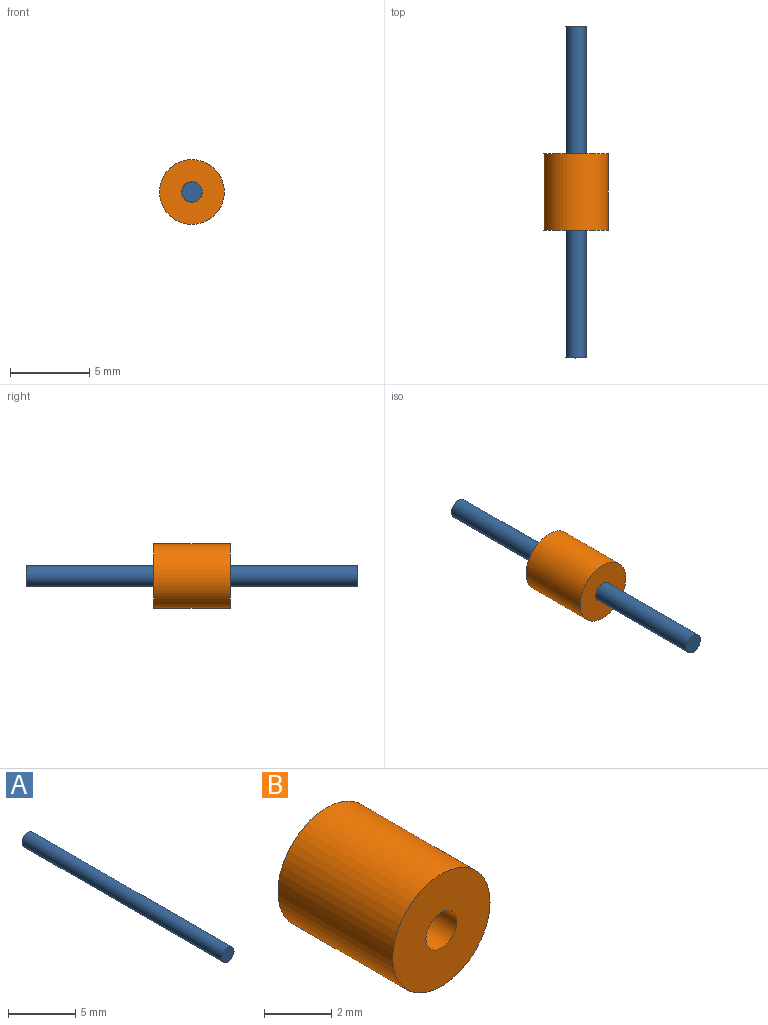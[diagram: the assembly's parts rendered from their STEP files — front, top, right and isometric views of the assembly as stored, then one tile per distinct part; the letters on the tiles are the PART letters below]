
ASSEMBLY  parts=2 mates=1
PART A: 3 faces, bbox 1.3x21x1.3 mm
  f0: cylinder r=0.64mm len=20.96mm, axis (0,1,0), area 83.6mm2, adj f1,f2
  f1: plane 1.27x1.27mm, normal (0,-1,0), area 1.3mm2, adj f0
  f2: plane 1.27x1.27mm, normal (0,1,0), area 1.3mm2, adj f0
PART B: 4 faces, bbox 4.1x4.8x4.1 mm
  f0: cylinder r=2.04mm len=4.83mm, axis (0,1,0), area 62mm2, adj f1,f2
  f1: plane 4.09x4.09mm, normal (0,-1,0), area 11.8mm2, adj f0,f3
  f2: plane 4.09x4.09mm, normal (0,1,0), area 11.8mm2, adj f0,f3
  f3: cylinder r=0.65mm len=4.83mm, axis (0,-1,0), area 19.6mm2, adj f1,f2
PLACE A rot(axis=(1,0,0),180deg) t=(-9.36,-17.65,-2.64)mm
PLACE B t=(-9.36,-4.76,-2.64)mm
MATE fastened A.f0 <-> B.f0  axis (0,-1,0) through (-9.36,3.31,-2.64)mm
